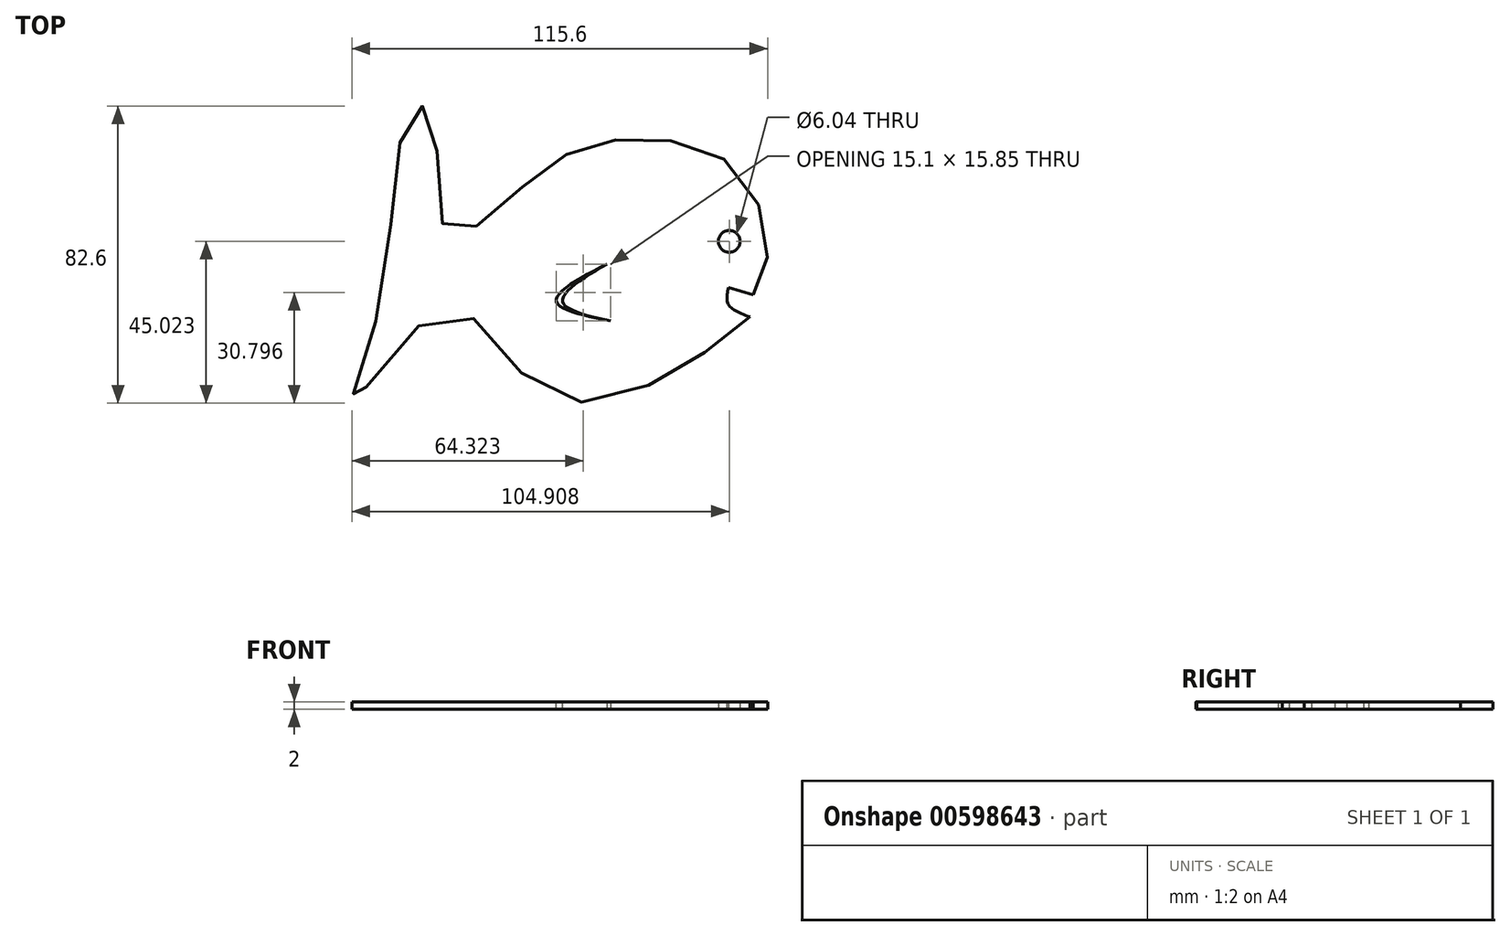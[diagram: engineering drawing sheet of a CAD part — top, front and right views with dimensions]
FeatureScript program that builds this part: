
annotation { "Feature Type Name" : "Feature", "Feature Type Description" : "" }
export const myFeature = defineFeature(function(context is Context, id is Id, definition is map)
    precondition{}
    {
        {
            var Q0;
            Q0=qCreatedBy(makeId("Top.planeOp"),FACE);
            var sketch = newSketch(context, id + "F0", { "sketchPlane" : qUnion([Q0])});
            skLineSegment(sketch, "E0", {"start": v(38.9, -17.28) * mm, "end": v(45.77, -19.38) * mm});
            skFitSpline(sketch, "E1", {"points": [v(38.9, -17.28) * mm, v(38.9, -22.06) * mm, v(44.82, -25.5) * mm], "startDerivative": vector(-2.47, -11.44) * mm, "endDerivative": vector(13.82, -5.17) * mm});
            skFitSpline(sketch, "E2", {"points": [v(45.77, -19.38) * mm, v(49.78, -6.59) * mm, v(40.23, 16.33) * mm, v(16.94, 23.96) * mm, v(-4.83, 20.34) * mm, v(-24.88, 4.87) * mm, v(-39.59, -1.62) * mm, v(-43.98, 31.8) * mm, v(-49.7, 30.65) * mm, v(-57.92, -21.3) * mm, v(-65.36, -49.36) * mm, v(-39.4, -23.58) * mm, v(-12.85, -46.12) * mm, v(21.33, -42.1) * mm, v(44.82, -25.5) * mm], "startDerivative": vector(115.39, 219.94) * mm, "endDerivative": vector(277.66, 229.66) * mm});
            skCircle(sketch, "E3", {"center": v(39.09, -4.49) * mm, "radius": 3.02 * mm});
            skFitSpline(sketch, "E4", {"points": [v(5.1, -10.79) * mm, v(-9.03, -21.1) * mm, v(6.05, -26.64) * mm], "startDerivative": vector(-42.6, -22.46) * mm, "endDerivative": vector(45.14, -9.14) * mm});
            skFitSpline(sketch, "E5", {"points": [v(5.1, -10.79) * mm, v(-7.28, -21.16) * mm, v(6.05, -26.64) * mm], "startDerivative": vector(-37.3, -22.46) * mm, "endDerivative": vector(39.95, -9.12) * mm});
            skSolve(sketch);
        }
        {
            var Q0;
            Q0=makeQuery(id+"F0.imprint","IMPRINT",FACE,{"disambiguationData":[TD([[makeQuery(id+"F0.imprint","IMPRINT",EDGE,{"derivedFrom":sQuery(id+"F0.wireOp",EDGE,"E0")}),1.0]])]});
            extrude(context, id + "F1", {"entities" : qUnion([Q0]), "depth" : 2 * mm, "offsetDistance" : 25 * mm});
        }
    });
